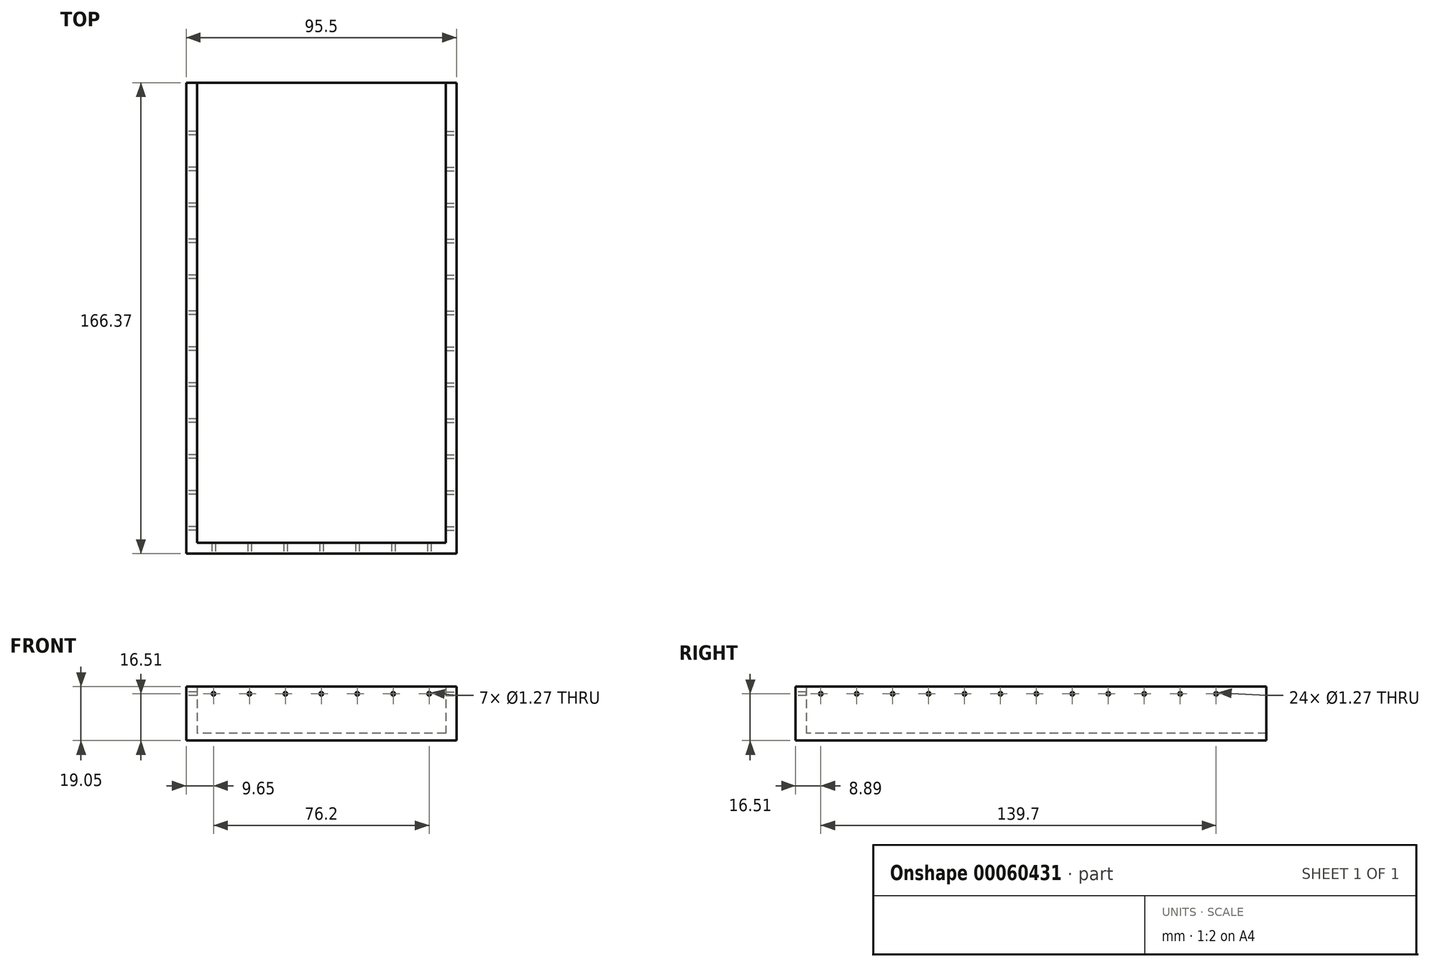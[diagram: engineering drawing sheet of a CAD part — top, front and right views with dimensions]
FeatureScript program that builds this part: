
annotation { "Feature Type Name" : "Feature", "Feature Type Description" : "" }
export const myFeature = defineFeature(function(context is Context, id is Id, definition is map)
    precondition{}
    {
        {
            var Q0;
            Q0=qCreatedBy(makeId("Top.planeOp"),FACE);
            var sketch = newSketch(context, id + "F0", { "sketchPlane" : qUnion([Q0])});
            skLineSegment(sketch, "E0.rect.bottom", {"start": v(43.94, 81.28) * mm, "end": v(-43.94, 81.28) * mm});
            skLineSegment(sketch, "E0.rect.top", {"start": v(43.94, -81.28) * mm, "end": v(-43.94, -81.28) * mm});
            skLineSegment(sketch, "E0.rect.left", {"start": v(43.94, 81.28) * mm, "end": v(43.94, -81.28) * mm});
            skLineSegment(sketch, "E0.rect.right", {"start": v(-43.94, 81.28) * mm, "end": v(-43.94, -81.28) * mm});
            skPoint(sketch, "E0.rect.middle", {"position": v(0, 0) * mm});
            skSolve(sketch);
        }
        {
            var Q0;
            Q0=makeQuery(id+"F0.imprint","IMPRINT",FACE,{"disambiguationData":[TD([[makeQuery(id+"F0.imprint","IMPRINT",EDGE,{"derivedFrom":sQuery(id+"F0.wireOp",EDGE,"E0.rect.bottom")}),1.0]])]});
            extrude(context, id + "F1", {"entities" : qUnion([Q0]), "depth" : 2.54 * mm});
        }
        {
            var Q0;
            Q0=qCreatedBy(makeId("Top.planeOp"),FACE);
            var sketch = newSketch(context, id + "F2", { "sketchPlane" : qUnion([Q0])});
            skLineSegment(sketch, "E1.bottom", {"start": v(-43.94, -81.28) * mm, "end": v(-47.75, -81.28) * mm});
            skLineSegment(sketch, "E1.top", {"start": v(-43.94, 81.28) * mm, "end": v(-47.75, 81.28) * mm});
            skLineSegment(sketch, "E1.left", {"start": v(-43.94, -81.28) * mm, "end": v(-43.94, 81.28) * mm});
            skLineSegment(sketch, "E1.right", {"start": v(-47.75, -81.28) * mm, "end": v(-47.75, 81.28) * mm});
            skLineSegment(sketch, "E2.bottom", {"start": v(43.94, -81.28) * mm, "end": v(47.75, -81.28) * mm});
            skLineSegment(sketch, "E2.top", {"start": v(43.94, 81.28) * mm, "end": v(47.75, 81.28) * mm});
            skLineSegment(sketch, "E2.left", {"start": v(43.94, -81.28) * mm, "end": v(43.94, 81.28) * mm});
            skLineSegment(sketch, "E2.right", {"start": v(47.75, -81.28) * mm, "end": v(47.75, 81.28) * mm});
            skSolve(sketch);
        }
        {
            var Q0;
            Q0 = qSketchRegion(id + "F2", true);
            extrude(context, id + "F3", {"entities" : qUnion([Q0]), "operationType" : NewBodyOperationType.ADD, "depth" : 19.05 * mm});
        }
        {
            var Q0;
            Q0=qCreatedBy(makeId("Top.planeOp"),FACE);
            var sketch = newSketch(context, id + "F4", { "sketchPlane" : qUnion([Q0])});
            skLineSegment(sketch, "E3.bottom", {"start": v(-47.75, -81.28) * mm, "end": v(47.75, -81.28) * mm});
            skLineSegment(sketch, "E3.top", {"start": v(-47.75, -85.1) * mm, "end": v(47.75, -85.1) * mm});
            skLineSegment(sketch, "E3.left", {"start": v(-47.75, -81.28) * mm, "end": v(-47.75, -85.1) * mm});
            skLineSegment(sketch, "E3.right", {"start": v(47.75, -81.28) * mm, "end": v(47.75, -85.1) * mm});
            skSolve(sketch);
        }
        {
            var Q0;
            Q0=makeQuery(id+"F4.imprint","IMPRINT",FACE,{"disambiguationData":[TD([[makeQuery(id+"F4.imprint","IMPRINT",EDGE,{"derivedFrom":sQuery(id+"F4.wireOp",EDGE,"E3.bottom")}),-1.0]])]});
            extrude(context, id + "F5", {"entities" : qUnion([Q0]), "operationType" : NewBodyOperationType.ADD, "depth" : 19.05 * mm});
        }
        {
            var Q0;
            Q0=makeQuery(id+"F5.boolean.opBoolean","MERGE",FACE,{"derivedFrom":[makeQuery(id+"F3.opExtrude","SWEPT_FACE",FACE,{"disambiguationData":[OSD([sQuery(id+"F2.wireOp",EDGE,"E2.right")])]}),makeQuery(id+"F5.opExtrude","SWEPT_FACE",FACE,{"disambiguationData":[OSD([sQuery(id+"F4.wireOp",EDGE,"E3.right")])]})]});
            var sketch = newSketch(context, id + "F6", { "sketchPlane" : qUnion([Q0])});
            skPoint(sketch, "E4", {"position": v(0, 16.51) * mm});
            skPoint(sketch, "E5.1.0.0", {"position": v(12.7, 16.51) * mm});
            skPoint(sketch, "E5.2.0.0", {"position": v(25.4, 16.51) * mm});
            skPoint(sketch, "E5.3.0.0", {"position": v(38.1, 16.51) * mm});
            skPoint(sketch, "E5.4.0.0", {"position": v(50.8, 16.51) * mm});
            skPoint(sketch, "E5.5.0.0", {"position": v(63.5, 16.51) * mm});
            skLineSegment(sketch, "E5.direction1", {"start": v(0, 16.51) * mm, "end": v(12.7, 16.51) * mm, "construction": true});
            skPoint(sketch, "E6.1.0.0", {"position": v(-12.7, 16.51) * mm});
            skPoint(sketch, "E6.2.0.0", {"position": v(-25.4, 16.51) * mm});
            skPoint(sketch, "E6.3.0.0", {"position": v(-38.1, 16.51) * mm});
            skPoint(sketch, "E6.4.0.0", {"position": v(-50.8, 16.51) * mm});
            skPoint(sketch, "E6.5.0.0", {"position": v(-63.5, 16.51) * mm});
            skPoint(sketch, "E6.6.0.0", {"position": v(-76.2, 16.51) * mm});
            skLineSegment(sketch, "E6.direction1", {"start": v(0, 16.51) * mm, "end": v(-12.7, 16.51) * mm, "construction": true});
            skSolve(sketch);
        }
        {
            var Q0;
            Q0=makeQuery(id+"F3.opExtrude","SWEPT_FACE",FACE,{"disambiguationData":[OSD([sQuery(id+"F2.wireOp",EDGE,"E1.right")])]});
            var sketch = newSketch(context, id + "F7", { "sketchPlane" : qUnion([Q0])});
            skPoint(sketch, "E7", {"position": v(0, 16.51) * mm});
            skPoint(sketch, "E8.1.0.0", {"position": v(12.7, 16.51) * mm});
            skPoint(sketch, "E8.2.0.0", {"position": v(25.4, 16.51) * mm});
            skPoint(sketch, "E8.3.0.0", {"position": v(38.1, 16.51) * mm});
            skPoint(sketch, "E8.4.0.0", {"position": v(50.8, 16.51) * mm});
            skPoint(sketch, "E8.5.0.0", {"position": v(63.5, 16.51) * mm});
            skPoint(sketch, "E8.6.0.0", {"position": v(76.2, 16.51) * mm});
            skLineSegment(sketch, "E8.direction1", {"start": v(0, 16.51) * mm, "end": v(12.7, 16.51) * mm, "construction": true});
            skPoint(sketch, "E9.1.0.0", {"position": v(-12.7, 16.51) * mm});
            skPoint(sketch, "E9.2.0.0", {"position": v(-25.4, 16.51) * mm});
            skPoint(sketch, "E9.3.0.0", {"position": v(-38.1, 16.51) * mm});
            skPoint(sketch, "E9.4.0.0", {"position": v(-50.8, 16.51) * mm});
            skPoint(sketch, "E9.5.0.0", {"position": v(-63.5, 16.51) * mm});
            skLineSegment(sketch, "E9.direction1", {"start": v(0, 16.51) * mm, "end": v(-12.7, 16.51) * mm, "construction": true});
            skSolve(sketch);
        }
        {
            var Q0;
            Q0=sQuery(id+"F6.wireOp",VERTEX,"E6.1.0.0");
            var Q1;
            Q1=sQuery(id+"F6.wireOp",VERTEX,"E4");
            var Q2;
            Q2=sQuery(id+"F6.wireOp",VERTEX,"E5.1.0.0");
            var Q3;
            Q3=sQuery(id+"F6.wireOp",VERTEX,"E5.2.0.0");
            var Q4;
            Q4=sQuery(id+"F6.wireOp",VERTEX,"E5.3.0.0");
            var Q5;
            Q5=sQuery(id+"F6.wireOp",VERTEX,"E5.4.0.0");
            var Q6;
            Q6=sQuery(id+"F6.wireOp",VERTEX,"E5.5.0.0");
            var Q7;
            Q7=sQuery(id+"F6.wireOp",VERTEX,"E6.2.0.0");
            var Q8;
            Q8=sQuery(id+"F6.wireOp",VERTEX,"E6.3.0.0");
            var Q9;
            Q9=sQuery(id+"F6.wireOp",VERTEX,"E6.4.0.0");
            var Q10;
            Q10=sQuery(id+"F6.wireOp",VERTEX,"E6.5.0.0");
            var Q11;
            Q11=sQuery(id+"F6.wireOp",VERTEX,"E6.6.0.0");
            var Q12;
            Q12=makeQuery(id+"F1.opExtrude","SWEPT_BODY",BODY,{"disambiguationData":[OSD([sQuery(id+"F0.wireOp",EDGE,"E0.rect.bottom"),sQuery(id+"F0.wireOp",EDGE,"E0.rect.top"),sQuery(id+"F0.wireOp",EDGE,"E0.rect.left"),sQuery(id+"F0.wireOp",EDGE,"E0.rect.right")])]});
            hole(context, id + "F8", {"style" : HoleStyle.SIMPLE, "holeDiameter" : 1.27 * mm, "endStyle" : HoleEndStyle.BLIND, "holeDepth" : 3.8 * mm, "locations" : qUnion([Q0, Q1, Q2, Q3, Q4, Q5, Q6, Q7, Q8, Q9, Q10, Q11]), "scope" : qUnion([Q12])});
        }
        {
            var Q0;
            Q0=sQuery(id+"F7.wireOp",VERTEX,"E9.5.0.0");
            var Q1;
            Q1=sQuery(id+"F7.wireOp",VERTEX,"E9.4.0.0");
            var Q2;
            Q2=sQuery(id+"F7.wireOp",VERTEX,"E9.3.0.0");
            var Q3;
            Q3=sQuery(id+"F7.wireOp",VERTEX,"E9.1.0.0");
            var Q4;
            Q4=sQuery(id+"F7.wireOp",VERTEX,"E7");
            var Q5;
            Q5=sQuery(id+"F7.wireOp",VERTEX,"E9.2.0.0");
            var Q6;
            Q6=sQuery(id+"F7.wireOp",VERTEX,"E8.1.0.0");
            var Q7;
            Q7=sQuery(id+"F7.wireOp",VERTEX,"E8.2.0.0");
            var Q8;
            Q8=sQuery(id+"F7.wireOp",VERTEX,"E8.3.0.0");
            var Q9;
            Q9=sQuery(id+"F7.wireOp",VERTEX,"E8.4.0.0");
            var Q10;
            Q10=sQuery(id+"F7.wireOp",VERTEX,"E8.5.0.0");
            var Q11;
            Q11=sQuery(id+"F7.wireOp",VERTEX,"E8.6.0.0");
            var Q12;
            Q12=makeQuery(id+"F1.opExtrude","SWEPT_BODY",BODY,{"disambiguationData":[OSD([sQuery(id+"F0.wireOp",EDGE,"E0.rect.bottom"),sQuery(id+"F0.wireOp",EDGE,"E0.rect.top"),sQuery(id+"F0.wireOp",EDGE,"E0.rect.left"),sQuery(id+"F0.wireOp",EDGE,"E0.rect.right")])]});
            hole(context, id + "F9", {"style" : HoleStyle.SIMPLE, "holeDiameter" : 1.27 * mm, "endStyle" : HoleEndStyle.BLIND, "holeDepth" : 3.8 * mm, "locations" : qUnion([Q0, Q1, Q2, Q3, Q4, Q5, Q6, Q7, Q8, Q9, Q10, Q11]), "scope" : qUnion([Q12])});
        }
        {
            var Q0;
            Q0=makeQuery(id+"F5.opExtrude","SWEPT_FACE",FACE,{"disambiguationData":[OSD([sQuery(id+"F4.wireOp",EDGE,"E3.top")])]});
            var sketch = newSketch(context, id + "F10", { "sketchPlane" : qUnion([Q0])});
            skPoint(sketch, "E10", {"position": v(0, 16.51) * mm});
            skPoint(sketch, "E11.1.0.0", {"position": v(12.7, 16.51) * mm});
            skPoint(sketch, "E11.2.0.0", {"position": v(25.4, 16.51) * mm});
            skPoint(sketch, "E11.3.0.0", {"position": v(38.1, 16.51) * mm});
            skLineSegment(sketch, "E11.direction1", {"start": v(0, 16.51) * mm, "end": v(12.7, 16.51) * mm, "construction": true});
            skPoint(sketch, "E12.1.0.0", {"position": v(-12.7, 16.51) * mm});
            skPoint(sketch, "E12.2.0.0", {"position": v(-25.4, 16.51) * mm});
            skPoint(sketch, "E12.3.0.0", {"position": v(-38.1, 16.51) * mm});
            skLineSegment(sketch, "E12.direction1", {"start": v(0, 16.51) * mm, "end": v(-12.7, 16.51) * mm, "construction": true});
            skSolve(sketch);
        }
        {
            var Q0;
            Q0=sQuery(id+"F10.wireOp",VERTEX,"E12.3.0.0");
            var Q1;
            Q1=sQuery(id+"F10.wireOp",VERTEX,"E12.2.0.0");
            var Q2;
            Q2=sQuery(id+"F10.wireOp",VERTEX,"E12.1.0.0");
            var Q3;
            Q3=sQuery(id+"F10.wireOp",VERTEX,"E10");
            var Q4;
            Q4=sQuery(id+"F10.wireOp",VERTEX,"E11.1.0.0");
            var Q5;
            Q5=sQuery(id+"F10.wireOp",VERTEX,"E11.2.0.0");
            var Q6;
            Q6=sQuery(id+"F10.wireOp",VERTEX,"E11.3.0.0");
            var Q7;
            Q7=makeQuery(id+"F1.opExtrude","SWEPT_BODY",BODY,{"disambiguationData":[OSD([sQuery(id+"F0.wireOp",EDGE,"E0.rect.bottom"),sQuery(id+"F0.wireOp",EDGE,"E0.rect.top"),sQuery(id+"F0.wireOp",EDGE,"E0.rect.left"),sQuery(id+"F0.wireOp",EDGE,"E0.rect.right")])]});
            hole(context, id + "F11", {"style" : HoleStyle.SIMPLE, "holeDiameter" : 1.27 * mm, "endStyle" : HoleEndStyle.BLIND, "holeDepth" : 3.8 * mm, "locations" : qUnion([Q0, Q1, Q2, Q3, Q4, Q5, Q6]), "scope" : qUnion([Q7])});
        }
    });
